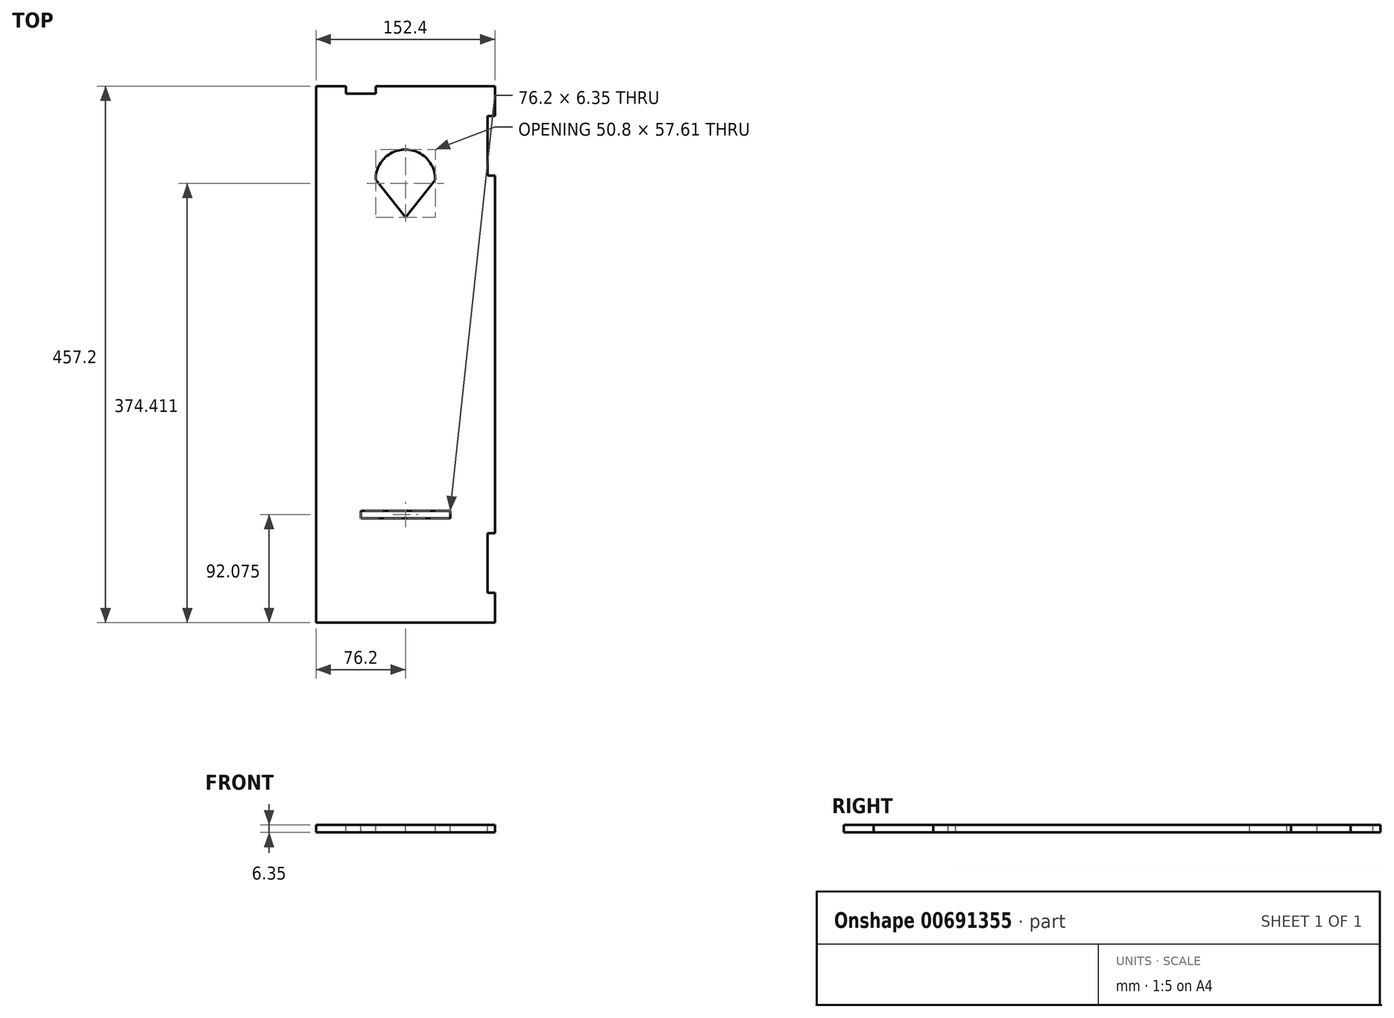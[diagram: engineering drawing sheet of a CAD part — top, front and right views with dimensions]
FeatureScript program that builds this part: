
annotation { "Feature Type Name" : "Feature", "Feature Type Description" : "" }
export const myFeature = defineFeature(function(context is Context, id is Id, definition is map)
    precondition{}
    {
        {
            var Q0;
            Q0=qCreatedBy(makeId("Top.planeOp"),FACE);
            var sketch = newSketch(context, id + "F0", { "sketchPlane" : qUnion([Q0])});
            skLineSegment(sketch, "E0.bottom", {"start": v(-76.2, 228.6) * mm, "end": v(76.2, 228.6) * mm});
            skLineSegment(sketch, "E0.top", {"start": v(-76.2, -228.6) * mm, "end": v(76.2, -228.6) * mm});
            skLineSegment(sketch, "E0.left", {"start": v(-76.2, 228.6) * mm, "end": v(-76.2, -228.6) * mm});
            skLineSegment(sketch, "E0.right", {"start": v(76.2, 228.6) * mm, "end": v(76.2, -228.6) * mm});
            skLineSegment(sketch, "E1", {"start": v(-76.2, 0) * mm, "end": v(76.2, 0) * mm, "construction": true});
            skSolve(sketch);
        }
        {
            var Q0;
            Q0=qSketchRegion(id+"F0",true);
            extrude(context, id + "F1", {"entities" : qUnion([Q0]), "depth" : 6.35 * mm, "offsetDistance" : 25.4 * mm});
        }
        {
            var Q0;
            Q0=makeQuery(id+"F1.opExtrude","CAP_FACE",FACE,{"disambiguationData":[OSD([sQuery(id+"F0.wireOp",EDGE,"E0.bottom"),sQuery(id+"F0.wireOp",EDGE,"E0.top"),sQuery(id+"F0.wireOp",EDGE,"E0.left"),sQuery(id+"F0.wireOp",EDGE,"E0.right")])],"isStart":false});
            var sketch = newSketch(context, id + "F2", { "sketchPlane" : qUnion([Q0])});
            skLineSegment(sketch, "E2.bottom", {"start": v(-50.8, 228.6) * mm, "end": v(-25.4, 228.6) * mm});
            skLineSegment(sketch, "E2.top", {"start": v(-50.8, 222.25) * mm, "end": v(-25.4, 222.25) * mm});
            skLineSegment(sketch, "E2.left", {"start": v(-50.8, 228.6) * mm, "end": v(-50.8, 222.25) * mm});
            skLineSegment(sketch, "E2.right", {"start": v(-25.4, 228.6) * mm, "end": v(-25.4, 222.25) * mm});
            skSolve(sketch);
        }
        {
            var Q0;
            Q0=qSketchRegion(id+"F2",true);
            extrude(context, id + "F3", {"entities" : qUnion([Q0]), "operationType" : NewBodyOperationType.REMOVE, "endBound" : BoundingType.THROUGH_ALL, "oppositeDirection" : true, "depth" : 25.4 * mm, "offsetDistance" : 25.4 * mm});
        }
        {
            var Q0;
            Q0=makeQuery(id+"F1.opExtrude","CAP_FACE",FACE,{"disambiguationData":[OSD([sQuery(id+"F0.wireOp",EDGE,"E0.bottom"),sQuery(id+"F0.wireOp",EDGE,"E0.top"),sQuery(id+"F0.wireOp",EDGE,"E0.left"),sQuery(id+"F0.wireOp",EDGE,"E0.right")])],"isStart":false});
            var sketch = newSketch(context, id + "F4", { "sketchPlane" : qUnion([Q0])});
            skLineSegment(sketch, "E3.bottom", {"start": v(76.2, 203.2) * mm, "end": v(69.85, 203.2) * mm});
            skLineSegment(sketch, "E3.top", {"start": v(76.2, 152.4) * mm, "end": v(69.85, 152.4) * mm});
            skLineSegment(sketch, "E3.left", {"start": v(76.2, 203.2) * mm, "end": v(76.2, 152.4) * mm});
            skLineSegment(sketch, "E3.right", {"start": v(69.85, 203.2) * mm, "end": v(69.85, 152.4) * mm});
            skLineSegment(sketch, "E4.MirrorCS", {"start": v(69.85, -203.2) * mm, "end": v(69.85, -152.4) * mm});
            skLineSegment(sketch, "E5.MirrorCS", {"start": v(76.2, -203.2) * mm, "end": v(76.2, -152.4) * mm});
            skLineSegment(sketch, "E6.MirrorCS", {"start": v(76.2, -152.4) * mm, "end": v(69.85, -152.4) * mm});
            skLineSegment(sketch, "E7.MirrorCS", {"start": v(76.2, -203.2) * mm, "end": v(69.85, -203.2) * mm});
            skSolve(sketch);
        }
        {
            var Q0;
            Q0=qSketchRegion(id+"F4",true);
            extrude(context, id + "F5", {"entities" : qUnion([Q0]), "operationType" : NewBodyOperationType.REMOVE, "oppositeDirection" : true, "depth" : 25.4 * mm, "offsetDistance" : 25.4 * mm});
        }
        {
            var Q0;
            Q0=makeQuery(id+"F1.opExtrude","CAP_FACE",FACE,{"disambiguationData":[OSD([sQuery(id+"F0.wireOp",EDGE,"E0.bottom"),sQuery(id+"F0.wireOp",EDGE,"E0.top"),sQuery(id+"F0.wireOp",EDGE,"E0.left"),sQuery(id+"F0.wireOp",EDGE,"E0.right")])],"isStart":false});
            var sketch = newSketch(context, id + "F6", { "sketchPlane" : qUnion([Q0])});
            skLineSegment(sketch, "E8.bottom", {"start": v(-38.1, -133.35) * mm, "end": v(38.1, -133.35) * mm});
            skLineSegment(sketch, "E8.top", {"start": v(-38.1, -139.7) * mm, "end": v(38.1, -139.7) * mm});
            skLineSegment(sketch, "E8.left", {"start": v(-38.1, -133.35) * mm, "end": v(-38.1, -139.7) * mm});
            skLineSegment(sketch, "E8.right", {"start": v(38.1, -133.35) * mm, "end": v(38.1, -139.7) * mm});
            skLineSegment(sketch, "E9", {"start": v(0, -139.7) * mm, "end": v(0, -228.6) * mm, "construction": true});
            skSolve(sketch);
        }
        {
            var Q0;
            Q0=qSketchRegion(id+"F6",true);
            extrude(context, id + "F7", {"entities" : qUnion([Q0]), "operationType" : NewBodyOperationType.REMOVE, "oppositeDirection" : true, "depth" : 25.4 * mm, "offsetDistance" : 25.4 * mm});
        }
        {
            var Q0;
            Q0=makeQuery(id+"F1.opExtrude","CAP_FACE",FACE,{"disambiguationData":[OSD([sQuery(id+"F0.wireOp",EDGE,"E0.bottom"),sQuery(id+"F0.wireOp",EDGE,"E0.top"),sQuery(id+"F0.wireOp",EDGE,"E0.left"),sQuery(id+"F0.wireOp",EDGE,"E0.right")])],"isStart":false});
            var sketch = newSketch(context, id + "F8", { "sketchPlane" : qUnion([Q0])});
            skLineSegment(sketch, "E10", {"start": v(-25.4, 148.9) * mm, "end": v(25.4, 148.9) * mm, "construction": true});
            skLineSegment(sketch, "E11", {"start": v(25.4, 148.9) * mm, "end": v(0, 117) * mm});
            skLineSegment(sketch, "E12", {"start": v(0, 117) * mm, "end": v(-25.4, 148.9) * mm});
            skArc(sketch, "E13", {"start": v(25.4, 148.9) * mm, "mid": v(0, 174.62) * mm, "end": v(-25.4, 148.9) * mm});
            skLineSegment(sketch, "E14", {"start": v(0, 174.62) * mm, "end": v(0, 228.6) * mm, "construction": true});
            skSolve(sketch);
        }
        {
            var Q0;
            Q0=qSketchRegion(id+"F8",true);
            extrude(context, id + "F9", {"entities" : qUnion([Q0]), "operationType" : NewBodyOperationType.REMOVE, "oppositeDirection" : true, "depth" : 25.4 * mm, "offsetDistance" : 25.4 * mm});
        }
    });
